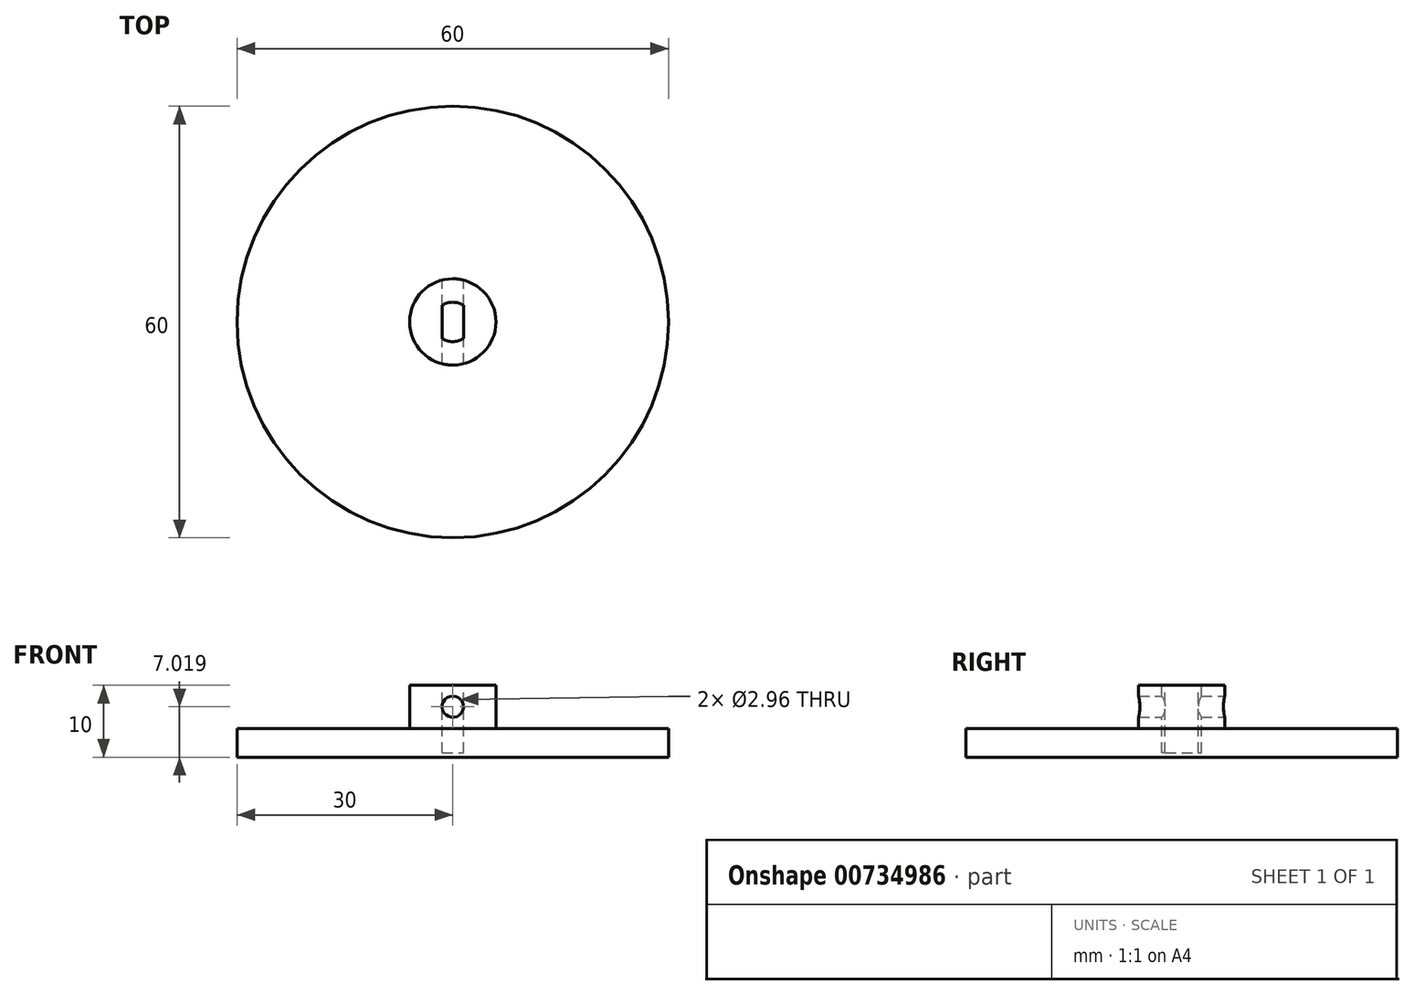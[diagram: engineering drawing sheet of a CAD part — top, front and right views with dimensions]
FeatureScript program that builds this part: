
annotation { "Feature Type Name" : "Feature", "Feature Type Description" : "" }
export const myFeature = defineFeature(function(context is Context, id is Id, definition is map)
    precondition{}
    {
        {
            var Q0;
            Q0=qCreatedBy(makeId("Top.planeOp"),FACE);
            var sketch = newSketch(context, id + "F0", { "sketchPlane" : qUnion([Q0])});
            skCircle(sketch, "E0", {"center": v(0, 0) * mm, "radius": 30 * mm});
            skSolve(sketch);
        }
        {
            var Q0;
            Q0 = qSketchRegion(id + "F0", true);
            extrude(context, id + "F1", {"entities" : qUnion([Q0]), "depth" : 4 * mm, "offsetDistance" : 25 * mm});
        }
        {
            var Q0;
            Q0=qCreatedBy(makeId("Top.planeOp"),FACE);
            var sketch = newSketch(context, id + "F2", { "sketchPlane" : qUnion([Q0])});
            skCircle(sketch, "E1", {"center": v(0, 0) * mm, "radius": 6 * mm});
            skSolve(sketch);
        }
        {
            var Q0;
            Q0 = qSketchRegion(id + "F2", true);
            extrude(context, id + "F3", {"entities" : qUnion([Q0]), "operationType" : NewBodyOperationType.ADD, "depth" : 10 * mm, "offsetDistance" : 25 * mm});
        }
        {
            var Q0;
            Q0=qCreatedBy(makeId("Front.planeOp"),FACE);
            var sketch = newSketch(context, id + "F4", { "sketchPlane" : qUnion([Q0])});
            skCircle(sketch, "E2", {"center": v(0, 7.02) * mm, "radius": 1.48 * mm});
            skSolve(sketch);
        }
        {
            var Q0;
            Q0 = qSketchRegion(id + "F4", true);
            extrude(context, id + "F5", {"entities" : qUnion([Q0]), "operationType" : NewBodyOperationType.REMOVE, "depth" : 25 * mm, "offsetDistance" : 25 * mm, "hasSecondDirection" : true, "secondDirectionOppositeDirection" : true, "secondDirectionDepth" : 25 * mm});
        }
        {
            var Q0;
            Q0=makeQuery(id+"F3.opExtrude","CAP_FACE",FACE,{"disambiguationData":[OSD([sQuery(id+"F2.wireOp",EDGE,"E1")])],"isStart":false});
            var sketch = newSketch(context, id + "F6", { "sketchPlane" : qUnion([Q0])});
            skLineSegment(sketch, "E3.left", {"start": v(-1.5, -2.3) * mm, "end": v(-1.5, 2.3) * mm});
            skLineSegment(sketch, "E3.right", {"start": v(1.5, -2.3) * mm, "end": v(1.5, 2.3) * mm});
            skPoint(sketch, "E3.middle", {"position": v(0, 0) * mm});
            skArc(sketch, "E4", {"start": v(-1.5, -2.3) * mm, "mid": v(0, -2.74) * mm, "end": v(1.5, -2.3) * mm});
            skArc(sketch, "E5.trimOffspring", {"start": v(1.5, 2.3) * mm, "mid": v(0, 2.74) * mm, "end": v(-1.5, 2.3) * mm});
            skSolve(sketch);
        }
        {
            var Q0;
            Q0 = qSketchRegion(id + "F6", true);
            extrude(context, id + "F7", {"entities" : qUnion([Q0]), "operationType" : NewBodyOperationType.REMOVE, "oppositeDirection" : true, "depth" : 9.4 * mm, "offsetDistance" : 25 * mm});
        }
    });
